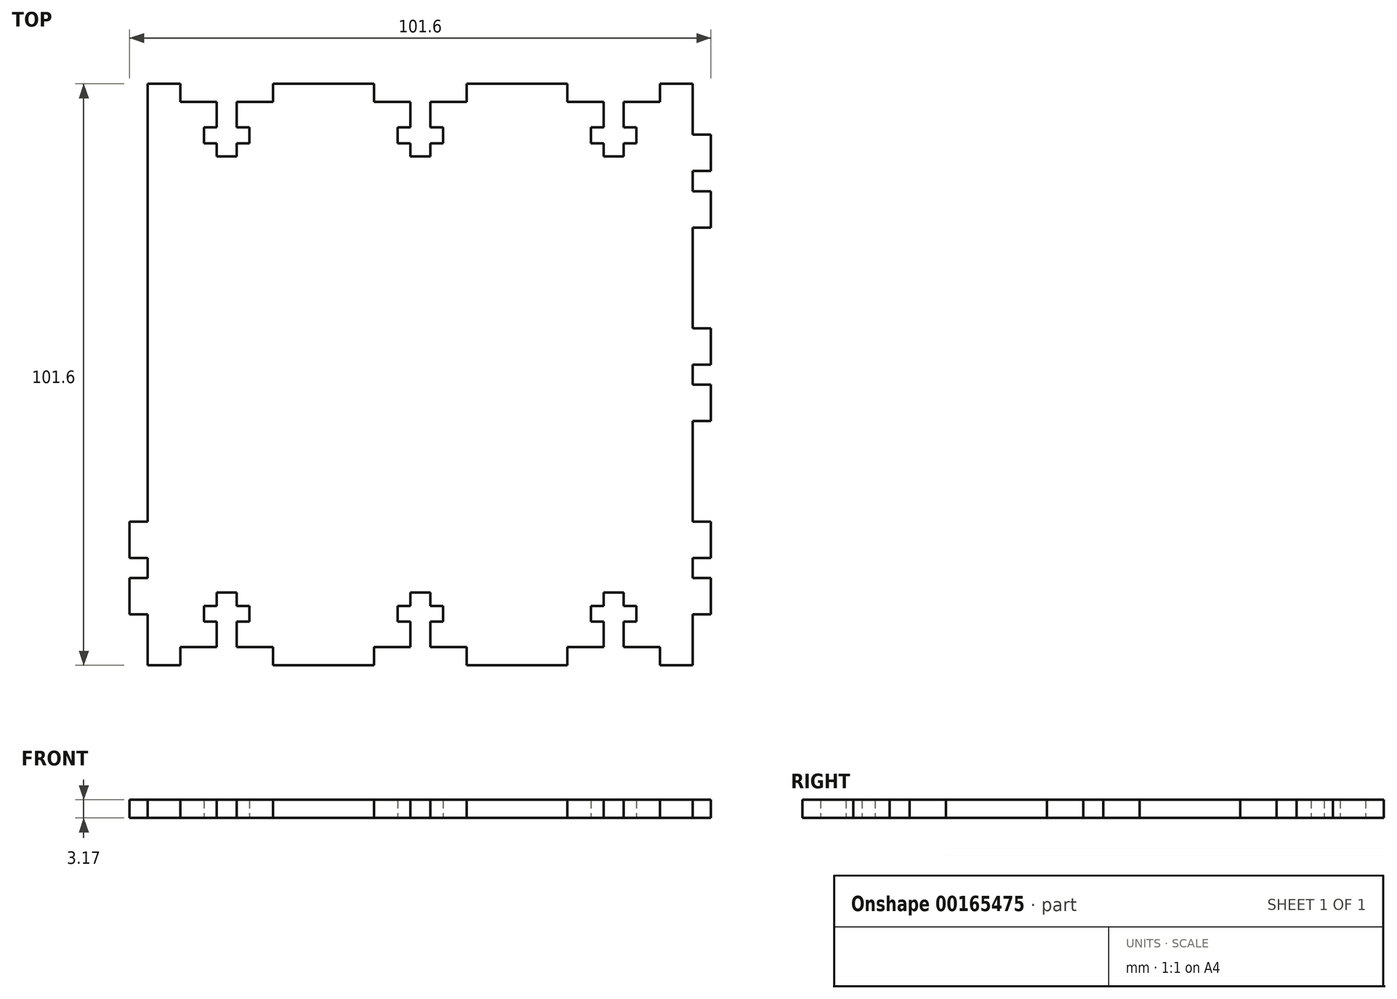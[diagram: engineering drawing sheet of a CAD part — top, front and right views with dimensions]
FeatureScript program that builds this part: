
annotation { "Feature Type Name" : "Feature", "Feature Type Description" : "" }
export const myFeature = defineFeature(function(context is Context, id is Id, definition is map)
    precondition{}
    {
        {
            var Q0;
            Q0=qCreatedBy(makeId("Top.planeOp"),FACE);
            var sketch = newSketch(context, id + "F0", { "sketchPlane" : qUnion([Q0])});
            skLineSegment(sketch, "E0.top", {"start": v(-48.14, 94.54) * mm, "end": v(53.46, 94.54) * mm});
            skLineSegment(sketch, "E0.left", {"start": v(-48.14, -7.06) * mm, "end": v(-48.14, 94.54) * mm});
            skLineSegment(sketch, "E0.right", {"start": v(53.46, -7.06) * mm, "end": v(53.46, 94.54) * mm});
            skLineSegment(sketch, "E1.bottom", {"start": v(-32.9, 94.54) * mm, "end": v(-29.4, 94.54) * mm});
            skLineSegment(sketch, "E1.top", {"start": v(-32.9, 81.84) * mm, "end": v(-29.4, 81.84) * mm});
            skLineSegment(sketch, "E1.left", {"start": v(-32.9, 94.54) * mm, "end": v(-32.9, 81.84) * mm});
            skLineSegment(sketch, "E1.right", {"start": v(-29.4, 94.54) * mm, "end": v(-29.4, 81.84) * mm});
            skLineSegment(sketch, "E2.bottom", {"start": v(-27.18, 84.14) * mm, "end": v(-35.11, 84.14) * mm});
            skLineSegment(sketch, "E2.top", {"start": v(-27.18, 86.92) * mm, "end": v(-35.11, 86.92) * mm});
            skLineSegment(sketch, "E2.left", {"start": v(-27.18, 84.14) * mm, "end": v(-27.18, 86.92) * mm});
            skLineSegment(sketch, "E2.right", {"start": v(-35.11, 84.14) * mm, "end": v(-35.11, 86.92) * mm});
            skLineSegment(sketch, "E3", {"start": v(-108, 43.74) * mm, "end": v(92.5, 43.74) * mm});
            skLineSegment(sketch, "E4.bottom", {"start": v(-39.25, 94.54) * mm, "end": v(-23.04, 94.54) * mm});
            skLineSegment(sketch, "E4.top", {"start": v(-39.25, 91.37) * mm, "end": v(-23.04, 91.37) * mm});
            skLineSegment(sketch, "E4.left", {"start": v(-39.25, 94.54) * mm, "end": v(-39.25, 91.37) * mm});
            skLineSegment(sketch, "E4.right", {"start": v(-23.04, 94.54) * mm, "end": v(-23.04, 91.37) * mm});
            skLineSegment(sketch, "E5.1.0.0", {"start": v(-5.44, 91.37) * mm, "end": v(10.76, 91.37) * mm});
            skLineSegment(sketch, "E5.1.0.1", {"start": v(4.41, 94.54) * mm, "end": v(4.41, 81.84) * mm});
            skLineSegment(sketch, "E5.1.0.2", {"start": v(0.9, 94.54) * mm, "end": v(0.9, 81.84) * mm});
            skLineSegment(sketch, "E5.1.0.3", {"start": v(-5.44, 94.54) * mm, "end": v(10.76, 94.54) * mm});
            skLineSegment(sketch, "E5.1.0.4", {"start": v(6.63, 86.92) * mm, "end": v(-1.3, 86.92) * mm});
            skLineSegment(sketch, "E5.1.0.6", {"start": v(-5.44, 94.54) * mm, "end": v(-5.44, 91.37) * mm});
            skLineSegment(sketch, "E5.1.0.7", {"start": v(0.9, 94.54) * mm, "end": v(4.41, 94.54) * mm});
            skLineSegment(sketch, "E5.1.0.8", {"start": v(10.76, 94.54) * mm, "end": v(10.76, 91.37) * mm});
            skLineSegment(sketch, "E5.1.0.9", {"start": v(0.9, 81.84) * mm, "end": v(4.41, 81.84) * mm});
            skLineSegment(sketch, "E5.1.0.10", {"start": v(6.63, 84.14) * mm, "end": v(6.63, 86.92) * mm});
            skLineSegment(sketch, "E5.1.0.11", {"start": v(6.63, 84.14) * mm, "end": v(-1.3, 84.14) * mm});
            skLineSegment(sketch, "E5.1.0.12", {"start": v(-1.3, 84.14) * mm, "end": v(-1.3, 86.92) * mm});
            skLineSegment(sketch, "E5.2.0.0", {"start": v(28.37, 91.37) * mm, "end": v(44.57, 91.37) * mm});
            skLineSegment(sketch, "E5.2.0.1", {"start": v(38.22, 94.54) * mm, "end": v(38.22, 81.84) * mm});
            skLineSegment(sketch, "E5.2.0.2", {"start": v(34.72, 94.54) * mm, "end": v(34.72, 81.84) * mm});
            skLineSegment(sketch, "E5.2.0.3", {"start": v(28.37, 94.54) * mm, "end": v(44.57, 94.54) * mm});
            skLineSegment(sketch, "E5.2.0.4", {"start": v(40.44, 86.92) * mm, "end": v(32.5, 86.92) * mm});
            skLineSegment(sketch, "E5.2.0.6", {"start": v(28.37, 94.54) * mm, "end": v(28.37, 91.37) * mm});
            skLineSegment(sketch, "E5.2.0.7", {"start": v(34.72, 94.54) * mm, "end": v(38.22, 94.54) * mm});
            skLineSegment(sketch, "E5.2.0.8", {"start": v(44.57, 94.54) * mm, "end": v(44.57, 91.37) * mm});
            skLineSegment(sketch, "E5.2.0.9", {"start": v(34.72, 81.84) * mm, "end": v(38.22, 81.84) * mm});
            skLineSegment(sketch, "E5.2.0.10", {"start": v(40.44, 84.14) * mm, "end": v(40.44, 86.92) * mm});
            skLineSegment(sketch, "E5.2.0.11", {"start": v(40.44, 84.14) * mm, "end": v(32.5, 84.14) * mm});
            skLineSegment(sketch, "E5.2.0.12", {"start": v(32.5, 84.14) * mm, "end": v(32.5, 86.92) * mm});
            skLineSegment(sketch, "E5.direction1", {"start": v(-32.9, 81.84) * mm, "end": v(0.9, 81.84) * mm, "construction": true});
            skLineSegment(sketch, "E6.MirrorCS", {"start": v(0.9, 5.64) * mm, "end": v(4.41, 5.64) * mm});
            skLineSegment(sketch, "E7.MirrorCS", {"start": v(-32.9, 5.64) * mm, "end": v(-29.4, 5.64) * mm});
            skLineSegment(sketch, "E8.MirrorCS", {"start": v(-23.04, -7.06) * mm, "end": v(-23.04, -3.88) * mm});
            skLineSegment(sketch, "E9.MirrorCS", {"start": v(-32.9, -7.06) * mm, "end": v(-29.4, -7.06) * mm});
            skLineSegment(sketch, "E10.MirrorCS", {"start": v(-35.11, 3.34) * mm, "end": v(-35.11, 0.56) * mm});
            skLineSegment(sketch, "E11.MirrorCS", {"start": v(-5.44, -7.06) * mm, "end": v(-5.44, -3.88) * mm});
            skLineSegment(sketch, "E12.MirrorCS", {"start": v(0.9, -7.06) * mm, "end": v(0.9, 5.64) * mm});
            skLineSegment(sketch, "E13.MirrorCS", {"start": v(-27.18, 3.34) * mm, "end": v(-27.18, 0.56) * mm});
            skLineSegment(sketch, "E14.MirrorCS", {"start": v(34.72, -7.06) * mm, "end": v(34.72, 5.64) * mm});
            skLineSegment(sketch, "E15.MirrorCS", {"start": v(0.9, -7.06) * mm, "end": v(4.41, -7.06) * mm});
            skLineSegment(sketch, "E16.MirrorCS", {"start": v(4.41, -7.06) * mm, "end": v(4.41, 5.64) * mm});
            skLineSegment(sketch, "E17.MirrorCS", {"start": v(40.44, 3.34) * mm, "end": v(40.44, 0.56) * mm});
            skLineSegment(sketch, "E18.MirrorCS", {"start": v(-39.25, -7.06) * mm, "end": v(-23.04, -7.06) * mm});
            skLineSegment(sketch, "E19.MirrorCS", {"start": v(-1.3, 3.34) * mm, "end": v(-1.3, 0.56) * mm});
            skLineSegment(sketch, "E20.MirrorCS", {"start": v(-5.44, -7.06) * mm, "end": v(10.76, -7.06) * mm});
            skLineSegment(sketch, "E21.MirrorCS", {"start": v(34.72, 5.64) * mm, "end": v(38.22, 5.64) * mm});
            skLineSegment(sketch, "E22.MirrorCS", {"start": v(28.37, -7.06) * mm, "end": v(28.37, -3.88) * mm});
            skLineSegment(sketch, "E23.MirrorCS", {"start": v(40.44, 3.34) * mm, "end": v(32.5, 3.34) * mm});
            skLineSegment(sketch, "E24.MirrorCS", {"start": v(28.37, -7.06) * mm, "end": v(44.57, -7.06) * mm});
            skLineSegment(sketch, "E25.MirrorCS", {"start": v(6.63, 3.34) * mm, "end": v(6.63, 0.56) * mm});
            skLineSegment(sketch, "E26.MirrorCS", {"start": v(10.76, -7.06) * mm, "end": v(10.76, -3.88) * mm});
            skLineSegment(sketch, "E27.MirrorCS", {"start": v(-32.9, -7.06) * mm, "end": v(-32.9, 5.64) * mm});
            skLineSegment(sketch, "E28.MirrorCS", {"start": v(-27.18, 3.34) * mm, "end": v(-35.11, 3.34) * mm});
            skLineSegment(sketch, "E29.MirrorCS", {"start": v(34.72, -7.06) * mm, "end": v(38.22, -7.06) * mm});
            skLineSegment(sketch, "E30.MirrorCS", {"start": v(44.57, -7.06) * mm, "end": v(44.57, -3.88) * mm});
            skLineSegment(sketch, "E31.MirrorCS", {"start": v(-39.25, -7.06) * mm, "end": v(-39.25, -3.88) * mm});
            skLineSegment(sketch, "E32.MirrorCS", {"start": v(32.5, 3.34) * mm, "end": v(32.5, 0.56) * mm});
            skLineSegment(sketch, "E33.MirrorCS", {"start": v(6.63, 3.34) * mm, "end": v(-1.3, 3.34) * mm});
            skLineSegment(sketch, "E34.MirrorCS", {"start": v(-29.4, -7.06) * mm, "end": v(-29.4, 5.64) * mm});
            skLineSegment(sketch, "E35.MirrorCS", {"start": v(38.22, -7.06) * mm, "end": v(38.22, 5.64) * mm});
            skLineSegment(sketch, "E36.MirrorCS", {"start": v(40.44, 0.56) * mm, "end": v(32.5, 0.56) * mm});
            skLineSegment(sketch, "E37.MirrorCS", {"start": v(-27.18, 0.56) * mm, "end": v(-35.11, 0.56) * mm});
            skLineSegment(sketch, "E38.MirrorCS", {"start": v(-32.9, 5.64) * mm, "end": v(0.9, 5.64) * mm, "construction": true});
            skLineSegment(sketch, "E39.MirrorCS", {"start": v(28.37, -3.88) * mm, "end": v(44.57, -3.88) * mm});
            skLineSegment(sketch, "E40.MirrorCS", {"start": v(-39.25, -3.88) * mm, "end": v(-23.04, -3.88) * mm});
            skLineSegment(sketch, "E41.MirrorCS", {"start": v(6.63, 0.56) * mm, "end": v(-1.3, 0.56) * mm});
            skLineSegment(sketch, "E42.MirrorCS", {"start": v(53.46, 94.54) * mm, "end": v(53.46, -7.06) * mm});
            skLineSegment(sketch, "E43.MirrorCS", {"start": v(-5.44, -3.88) * mm, "end": v(10.76, -3.88) * mm});
            skLineSegment(sketch, "E44.MirrorCS", {"start": v(-48.14, -7.06) * mm, "end": v(53.46, -7.06) * mm});
            skLineSegment(sketch, "E45.MirrorCS", {"start": v(-48.14, 94.54) * mm, "end": v(-48.14, -7.06) * mm});
            skLineSegment(sketch, "E46.bottom", {"start": v(-48.14, 94.54) * mm, "end": v(-44.96, 94.54) * mm});
            skLineSegment(sketch, "E46.top", {"start": v(-48.14, -7.06) * mm, "end": v(-44.96, -7.06) * mm});
            skLineSegment(sketch, "E46.right", {"start": v(-44.96, 94.54) * mm, "end": v(-44.96, -7.06) * mm});
            skLineSegment(sketch, "E47.bottom", {"start": v(53.46, -7.06) * mm, "end": v(50.29, -7.06) * mm});
            skLineSegment(sketch, "E47.top", {"start": v(53.46, 94.54) * mm, "end": v(50.29, 94.54) * mm});
            skLineSegment(sketch, "E47.right", {"start": v(50.29, -7.06) * mm, "end": v(50.29, 94.54) * mm});
            skLineSegment(sketch, "E48.bottom", {"start": v(-44.96, 1.83) * mm, "end": v(-48.14, 1.83) * mm});
            skLineSegment(sketch, "E48.top", {"start": v(-44.96, 8.18) * mm, "end": v(-48.14, 8.18) * mm});
            skLineSegment(sketch, "E48.left", {"start": v(-44.96, 1.83) * mm, "end": v(-44.96, 8.18) * mm});
            skLineSegment(sketch, "E48.right", {"start": v(-48.14, 1.83) * mm, "end": v(-48.14, 8.18) * mm});
            skLineSegment(sketch, "E49.top", {"start": v(-44.96, 11.69) * mm, "end": v(-48.14, 11.69) * mm});
            skLineSegment(sketch, "E49.left", {"start": v(-44.96, 8.18) * mm, "end": v(-44.96, 11.69) * mm});
            skLineSegment(sketch, "E49.right", {"start": v(-48.14, 8.18) * mm, "end": v(-48.14, 11.69) * mm});
            skLineSegment(sketch, "E50.top", {"start": v(-44.96, 18.04) * mm, "end": v(-48.14, 18.04) * mm});
            skLineSegment(sketch, "E50.left", {"start": v(-44.96, 11.69) * mm, "end": v(-44.96, 18.04) * mm});
            skLineSegment(sketch, "E50.right", {"start": v(-48.14, 11.69) * mm, "end": v(-48.14, 18.04) * mm});
            skLineSegment(sketch, "E51.0.1.0", {"start": v(-48.14, 41.99) * mm, "end": v(-48.14, 45.5) * mm});
            skLineSegment(sketch, "E51.0.1.1", {"start": v(-44.96, 35.64) * mm, "end": v(-44.96, 41.99) * mm});
            skLineSegment(sketch, "E51.0.1.2", {"start": v(-44.96, 35.64) * mm, "end": v(-48.14, 35.64) * mm});
            skLineSegment(sketch, "E51.0.1.3", {"start": v(-48.14, 45.5) * mm, "end": v(-48.14, 51.84) * mm});
            skLineSegment(sketch, "E51.0.1.4", {"start": v(-44.96, 41.99) * mm, "end": v(-44.96, 45.5) * mm});
            skLineSegment(sketch, "E51.0.1.5", {"start": v(-44.96, 45.5) * mm, "end": v(-48.14, 45.5) * mm});
            skLineSegment(sketch, "E51.0.1.6", {"start": v(-44.96, 45.5) * mm, "end": v(-44.96, 51.84) * mm});
            skLineSegment(sketch, "E51.0.1.7", {"start": v(-48.14, 35.64) * mm, "end": v(-48.14, 41.99) * mm});
            skLineSegment(sketch, "E51.0.1.8", {"start": v(-44.96, 41.99) * mm, "end": v(-48.14, 41.99) * mm});
            skLineSegment(sketch, "E51.0.1.9", {"start": v(-44.96, 51.84) * mm, "end": v(-48.14, 51.84) * mm});
            skLineSegment(sketch, "E51.0.1.10", {"start": v(-44.96, 41.99) * mm, "end": v(-48.14, 41.99) * mm});
            skLineSegment(sketch, "E51.0.1.11", {"start": v(-44.96, 45.5) * mm, "end": v(-48.14, 45.5) * mm});
            skLineSegment(sketch, "E51.0.2.0", {"start": v(-48.14, 75.8) * mm, "end": v(-48.14, 79.3) * mm});
            skLineSegment(sketch, "E51.0.2.1", {"start": v(-44.96, 69.45) * mm, "end": v(-44.96, 75.8) * mm});
            skLineSegment(sketch, "E51.0.2.2", {"start": v(-44.96, 69.45) * mm, "end": v(-48.14, 69.45) * mm});
            skLineSegment(sketch, "E51.0.2.3", {"start": v(-48.14, 79.3) * mm, "end": v(-48.14, 85.65) * mm});
            skLineSegment(sketch, "E51.0.2.4", {"start": v(-44.96, 75.8) * mm, "end": v(-44.96, 79.3) * mm});
            skLineSegment(sketch, "E51.0.2.5", {"start": v(-44.96, 79.3) * mm, "end": v(-48.14, 79.3) * mm});
            skLineSegment(sketch, "E51.0.2.6", {"start": v(-44.96, 79.3) * mm, "end": v(-44.96, 85.65) * mm});
            skLineSegment(sketch, "E51.0.2.7", {"start": v(-48.14, 69.45) * mm, "end": v(-48.14, 75.8) * mm});
            skLineSegment(sketch, "E51.0.2.8", {"start": v(-44.96, 75.8) * mm, "end": v(-48.14, 75.8) * mm});
            skLineSegment(sketch, "E51.0.2.9", {"start": v(-44.96, 85.65) * mm, "end": v(-48.14, 85.65) * mm});
            skLineSegment(sketch, "E51.0.2.10", {"start": v(-44.96, 75.8) * mm, "end": v(-48.14, 75.8) * mm});
            skLineSegment(sketch, "E51.0.2.11", {"start": v(-44.96, 79.3) * mm, "end": v(-48.14, 79.3) * mm});
            skLineSegment(sketch, "E51.direction1", {"start": v(-48.14, 1.83) * mm, "end": v(-22.74, 1.83) * mm, "construction": true});
            skLineSegment(sketch, "E51.direction2", {"start": v(-48.14, 1.83) * mm, "end": v(-48.14, 35.64) * mm, "construction": true});
            skLineSegment(sketch, "E52", {"start": v(2.66, 112.42) * mm, "end": v(2.66, 100.35) * mm});
            skLineSegment(sketch, "E53.MirrorCS", {"start": v(50.29, 75.8) * mm, "end": v(53.46, 75.8) * mm});
            skLineSegment(sketch, "E54.MirrorCS", {"start": v(50.29, 11.69) * mm, "end": v(53.46, 11.69) * mm});
            skLineSegment(sketch, "E55.MirrorCS", {"start": v(50.29, 79.3) * mm, "end": v(53.46, 79.3) * mm});
            skLineSegment(sketch, "E56.MirrorCS", {"start": v(50.29, 8.18) * mm, "end": v(53.46, 8.18) * mm});
            skLineSegment(sketch, "E57.MirrorCS", {"start": v(50.29, 45.5) * mm, "end": v(53.46, 45.5) * mm});
            skLineSegment(sketch, "E58.MirrorCS", {"start": v(50.29, 41.99) * mm, "end": v(53.46, 41.99) * mm});
            skLineSegment(sketch, "E59.MirrorCS", {"start": v(53.46, 75.8) * mm, "end": v(53.46, 79.3) * mm});
            skLineSegment(sketch, "E60.MirrorCS", {"start": v(53.46, 8.18) * mm, "end": v(53.46, 11.69) * mm});
            skLineSegment(sketch, "E61.MirrorCS", {"start": v(50.29, 41.99) * mm, "end": v(50.29, 45.5) * mm});
            skLineSegment(sketch, "E62.MirrorCS", {"start": v(50.29, 1.83) * mm, "end": v(53.46, 1.83) * mm});
            skLineSegment(sketch, "E63.MirrorCS", {"start": v(50.29, 8.18) * mm, "end": v(50.29, 11.69) * mm});
            skLineSegment(sketch, "E64.MirrorCS", {"start": v(53.46, 41.99) * mm, "end": v(53.46, 45.5) * mm});
            skLineSegment(sketch, "E65.MirrorCS", {"start": v(53.46, 1.83) * mm, "end": v(53.46, 8.18) * mm});
            skLineSegment(sketch, "E66.MirrorCS", {"start": v(50.29, 75.8) * mm, "end": v(50.29, 79.3) * mm});
            skLineSegment(sketch, "E67.MirrorCS", {"start": v(50.29, 35.64) * mm, "end": v(53.46, 35.64) * mm});
            skLineSegment(sketch, "E68.MirrorCS", {"start": v(53.46, 35.64) * mm, "end": v(53.46, 41.99) * mm});
            skLineSegment(sketch, "E69.MirrorCS", {"start": v(50.29, 18.04) * mm, "end": v(53.46, 18.04) * mm});
            skLineSegment(sketch, "E70.MirrorCS", {"start": v(50.29, 69.45) * mm, "end": v(50.29, 75.8) * mm});
            skLineSegment(sketch, "E71.MirrorCS", {"start": v(50.29, 11.69) * mm, "end": v(50.29, 18.04) * mm});
            skLineSegment(sketch, "E72.MirrorCS", {"start": v(53.46, 45.5) * mm, "end": v(53.46, 51.84) * mm});
            skLineSegment(sketch, "E73.MirrorCS", {"start": v(53.46, 69.45) * mm, "end": v(53.46, 75.8) * mm});
            skLineSegment(sketch, "E74.MirrorCS", {"start": v(50.29, 79.3) * mm, "end": v(50.29, 85.65) * mm});
            skLineSegment(sketch, "E75.MirrorCS", {"start": v(50.29, 69.45) * mm, "end": v(53.46, 69.45) * mm});
            skLineSegment(sketch, "E76.MirrorCS", {"start": v(50.29, 35.64) * mm, "end": v(50.29, 41.99) * mm});
            skLineSegment(sketch, "E77.MirrorCS", {"start": v(50.29, 51.84) * mm, "end": v(53.46, 51.84) * mm});
            skLineSegment(sketch, "E78.MirrorCS", {"start": v(50.29, 1.83) * mm, "end": v(50.29, 8.18) * mm});
            skLineSegment(sketch, "E79.MirrorCS", {"start": v(50.29, 45.5) * mm, "end": v(50.29, 51.84) * mm});
            skLineSegment(sketch, "E80.MirrorCS", {"start": v(53.46, 11.69) * mm, "end": v(53.46, 18.04) * mm});
            skLineSegment(sketch, "E81.MirrorCS", {"start": v(53.46, 79.3) * mm, "end": v(53.46, 85.65) * mm});
            skLineSegment(sketch, "E82.MirrorCS", {"start": v(50.29, 85.65) * mm, "end": v(53.46, 85.65) * mm});
            skLineSegment(sketch, "E83.MirrorCS", {"start": v(53.46, 1.83) * mm, "end": v(53.46, 35.64) * mm, "construction": true});
            skLineSegment(sketch, "E84.MirrorCS", {"start": v(50.29, 94.54) * mm, "end": v(50.29, -7.06) * mm});
            skSolve(sketch);
        }
        {
            var Q0;
            {var subQ41=sQuery(id+"F0.wireOp",EDGE,"E1.top");Q0=makeQuery(id+"F0.imprint","IMPRINT",FACE,{"disambiguationData":[TD([[makeQuery(id+"F0.imprint","IMPRINT",EDGE,{"derivedFrom":subQ41}),-1.0]])]});}
            var Q1;
            {var subQ55=sQuery(id+"F0.wireOp",EDGE,"E6.MirrorCS");Q1=makeQuery(id+"F0.imprint","IMPRINT",FACE,{"disambiguationData":[TD([[makeQuery(id+"F0.imprint","IMPRINT",EDGE,{"derivedFrom":subQ55}),1.0]])]});}
            var Q2;
            Q2=makeQuery(id+"F0.imprint","IMPRINT",FACE,{"disambiguationData":[TD([[makeQuery(id+"F0.imprint","IMPRINT",EDGE,{"derivedFrom":sQuery(id+"F0.wireOp",EDGE,"E51.0.1.3")}),-1.0]])]});
            var Q3;
            Q3=makeQuery(id+"F0.imprint","IMPRINT",FACE,{"disambiguationData":[TD([[makeQuery(id+"F0.imprint","IMPRINT",EDGE,{"derivedFrom":sQuery(id+"F0.wireOp",EDGE,"E51.0.2.1")}),1.0]])]});
            var Q4;
            Q4=makeQuery(id+"F0.imprint","IMPRINT",FACE,{"disambiguationData":[TD([[makeQuery(id+"F0.imprint","IMPRINT",EDGE,{"derivedFrom":sQuery(id+"F0.wireOp",EDGE,"E51.0.2.3")}),-1.0]])]});
            var Q5;
            Q5=makeQuery(id+"F0.imprint","IMPRINT",FACE,{"disambiguationData":[TD([[makeQuery(id+"F0.imprint","IMPRINT",EDGE,{"derivedFrom":sQuery(id+"F0.wireOp",EDGE,"E51.0.1.1")}),1.0]])]});
            var Q6;
            Q6=makeQuery(id+"F0.imprint","IMPRINT",FACE,{"disambiguationData":[TD([[makeQuery(id+"F0.imprint","IMPRINT",EDGE,{"derivedFrom":sQuery(id+"F0.wireOp",EDGE,"E49.top")}),-1.0]])]});
            var Q7;
            Q7=makeQuery(id+"F0.imprint","IMPRINT",FACE,{"disambiguationData":[TD([[makeQuery(id+"F0.imprint","IMPRINT",EDGE,{"derivedFrom":sQuery(id+"F0.wireOp",EDGE,"E48.bottom")}),-1.0]])]});
            var Q8;
            {var subQ0=sQuery(id+"F0.wireOp",EDGE,"E62.MirrorCS");Q8=makeQuery(id+"F0.imprint","IMPRINT",FACE,{"disambiguationData":[TD([[makeQuery(id+"F0.imprint","IMPRINT",EDGE,{"derivedFrom":subQ0}),1.0]])]});}
            var Q9;
            {var subQ0=sQuery(id+"F0.wireOp",EDGE,"E54.MirrorCS");Q9=makeQuery(id+"F0.imprint","IMPRINT",FACE,{"disambiguationData":[TD([[makeQuery(id+"F0.imprint","IMPRINT",EDGE,{"derivedFrom":subQ0}),1.0]])]});}
            var Q10;
            {var subQ0=sQuery(id+"F0.wireOp",EDGE,"E58.MirrorCS");Q10=makeQuery(id+"F0.imprint","IMPRINT",FACE,{"disambiguationData":[TD([[makeQuery(id+"F0.imprint","IMPRINT",EDGE,{"derivedFrom":subQ0}),-1.0]])]});}
            var Q11;
            {var subQ0=sQuery(id+"F0.wireOp",EDGE,"E57.MirrorCS");Q11=makeQuery(id+"F0.imprint","IMPRINT",FACE,{"disambiguationData":[TD([[makeQuery(id+"F0.imprint","IMPRINT",EDGE,{"derivedFrom":subQ0}),1.0]])]});}
            var Q12;
            {var subQ0=sQuery(id+"F0.wireOp",EDGE,"E53.MirrorCS");Q12=makeQuery(id+"F0.imprint","IMPRINT",FACE,{"disambiguationData":[TD([[makeQuery(id+"F0.imprint","IMPRINT",EDGE,{"derivedFrom":subQ0}),-1.0]])]});}
            var Q13;
            {var subQ0=sQuery(id+"F0.wireOp",EDGE,"E55.MirrorCS");Q13=makeQuery(id+"F0.imprint","IMPRINT",FACE,{"disambiguationData":[TD([[makeQuery(id+"F0.imprint","IMPRINT",EDGE,{"derivedFrom":subQ0}),1.0]])]});}
            extrude(context, id + "F1", {"entities" : qUnion([Q0, Q1, Q2, Q3, Q4, Q5, Q6, Q7, Q8, Q9, Q10, Q11, Q12, Q13]), "depth" : 3.17 * mm});
        }
    });
